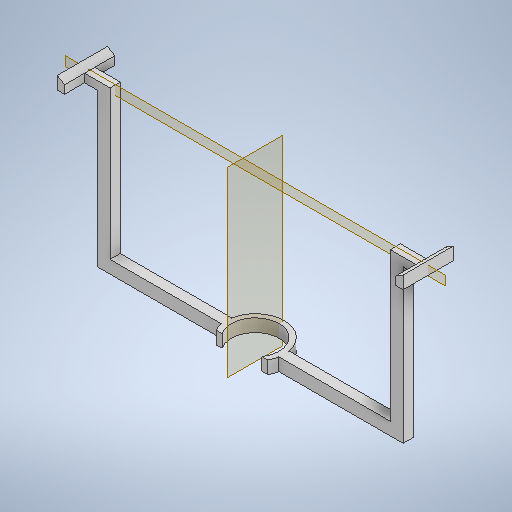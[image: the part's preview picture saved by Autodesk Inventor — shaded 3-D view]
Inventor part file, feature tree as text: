
AUTODESK INVENTOR PART (.ipt)
format: ipt  version: 2025.1 (Build 291241000, 241)  size: 324,096 bytes
history: native  units: mm
features: extrude x6, sketch x6, plane x2
ambient origin geometry x8: Origin, YZ Plane, XZ Plane, XY Plane, X Axis, Y Axis, Z Axis, Center Point
bodies: Volumenkörper1 (feature_tree)
feature tree (14):
  extrude  "Extrusion1"  Depth=2.85mm
  plane  "Arbeitsebene1"
  extrude  "Extrusion2"  Depth=2.85mm
  extrude  "Extrusion7"  Depth=5.0mm
  extrude  "Extrusion8"  Depth=63.25mm TaperAngle=0.0deg
  plane  "Arbeitsebene2"
  extrude  "Extrusion9"  Depth=5.0mm
  extrude  "Extrusion10"  TaperAngle=0.0deg  [1 undecoded]
  sketch  "Skizze1"  dims[d0=135.6mm d1=4.0mm d2=3.25mm d3=0.0mm d4=2.85mm]
  sketch  "Skizze2"  dims[d5=1.75mm d6=2.85mm]
  sketch  "Skizze7"  dims[d7=19.7mm d8=0.0mm d27=5.0mm]
  sketch  "Skizze8"  dims[d28=5.0mm d29=63.25mm d30=0.0mm]
  sketch  "Skizze9"  dims[d31=5.0mm d32=5.0mm]
  sketch  "Skizze10"  dims[d34=58.25mm d35=0.0mm d36=0.0mm d38=21.6mm d39=0.0mm d40=0.0mm d41=18.8mm d42=22.8mm d43=5.0mm d44=0.0mm d15=0.5mm d16=0.872665mm d17=0.5mm d18=0.872665mm]
note: 1 required parameter value undecoded (feature->parameter linkage not recoverable at this tier; creation-order binding heuristic only, values carry confidence <= 0.55)
